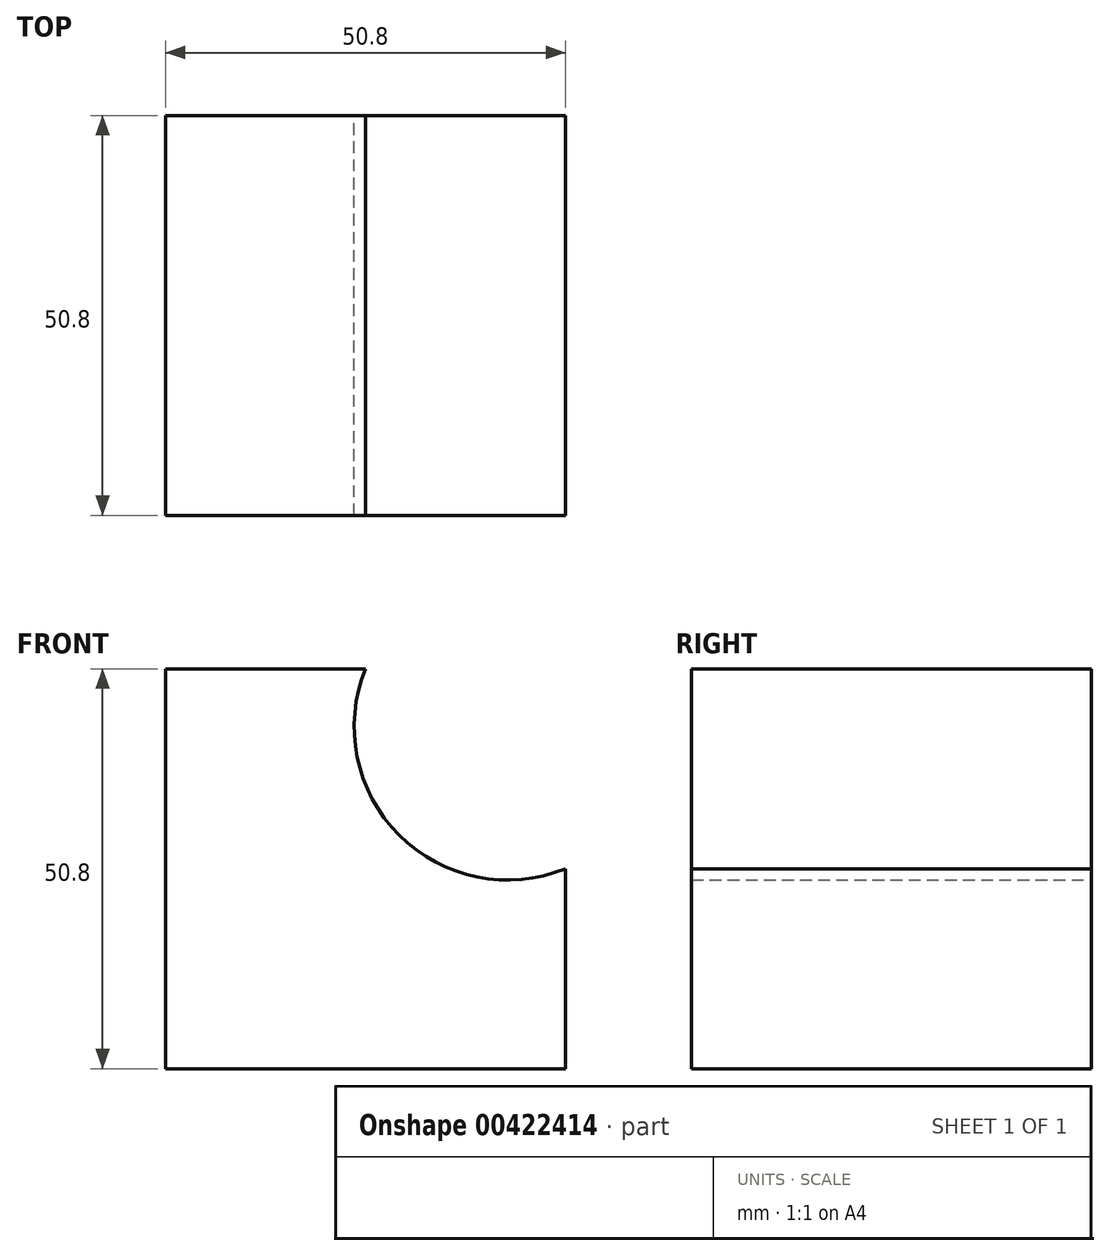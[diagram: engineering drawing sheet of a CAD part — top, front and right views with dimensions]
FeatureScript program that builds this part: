
annotation { "Feature Type Name" : "Feature", "Feature Type Description" : "" }
export const myFeature = defineFeature(function(context is Context, id is Id, definition is map)
    precondition{}
    {
        {
            var Q0;
            Q0=qCreatedBy(makeId("Front.planeOp"),FACE);
            var sketch = newSketch(context, id + "F0", { "sketchPlane" : qUnion([Q0])});
            skLineSegment(sketch, "E0", {"start": v(0, 0) * mm, "end": v(-50.8, 0) * mm});
            skLineSegment(sketch, "E1", {"start": v(-50.8, 0) * mm, "end": v(-50.8, 50.8) * mm});
            skLineSegment(sketch, "E2", {"start": v(-50.8, 50.8) * mm, "end": v(-25.4, 50.8) * mm});
            skLineSegment(sketch, "E3", {"start": v(0, 0) * mm, "end": v(0, 25.4) * mm});
            skArc(sketch, "E4", {"start": v(-25.4, 50.8) * mm, "mid": v(-21.13, 29.67) * mm, "end": v(0, 25.4) * mm});
            skSolve(sketch);
        }
        {
            var Q0;
            Q0 = qSketchRegion(id + "F0", true);
            extrude(context, id + "F1", {"entities" : qUnion([Q0]), "depth" : 50.8 * mm});
        }
    });
